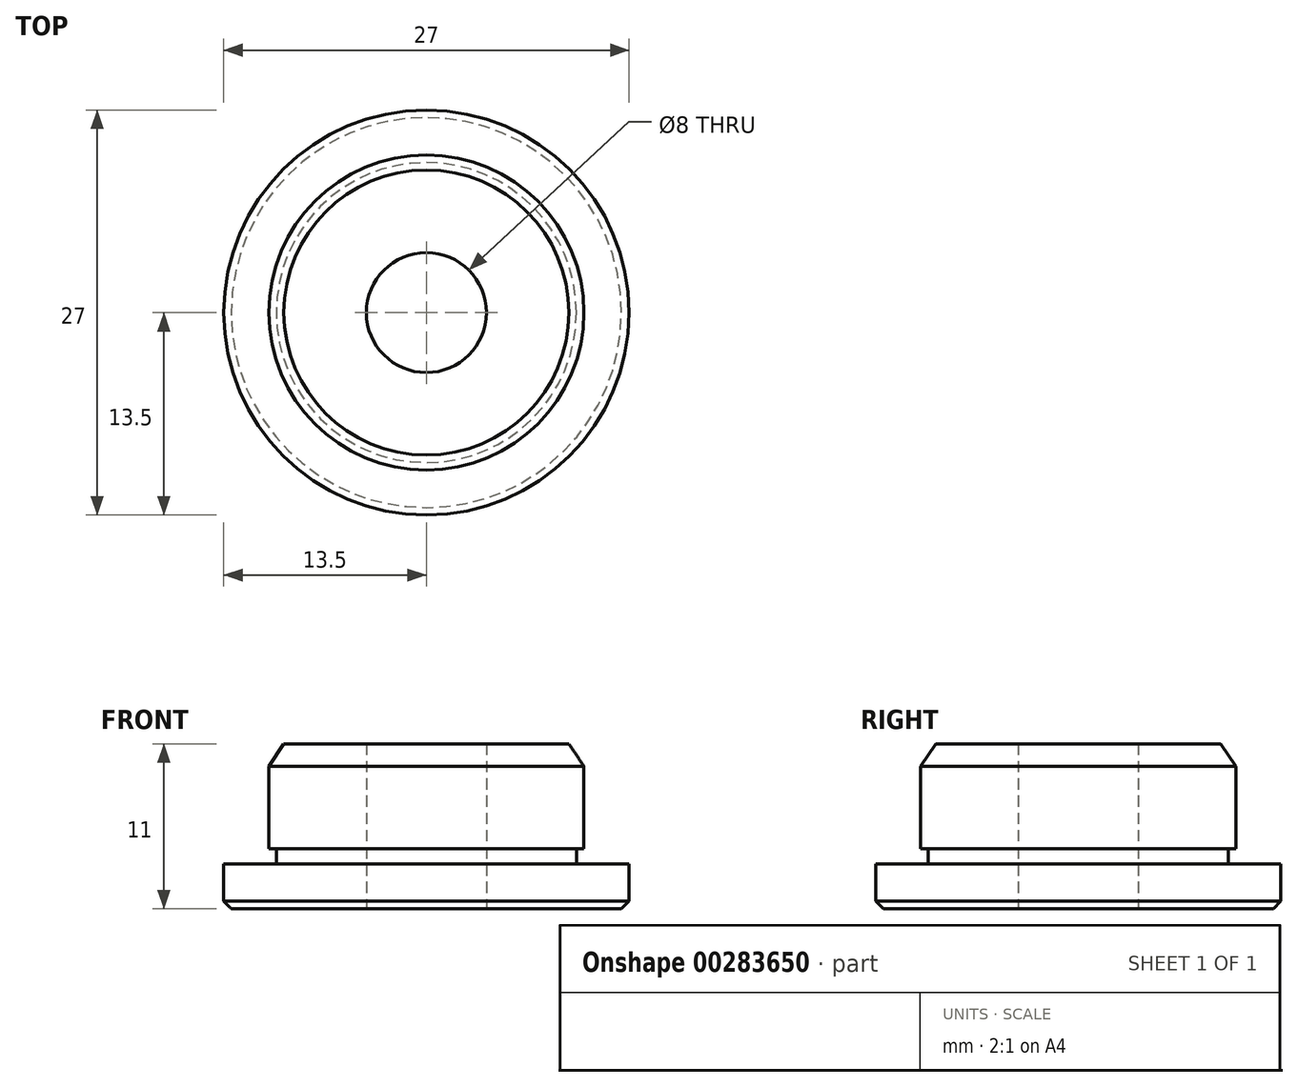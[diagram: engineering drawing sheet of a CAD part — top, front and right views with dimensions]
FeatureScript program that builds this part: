
annotation { "Feature Type Name" : "Feature", "Feature Type Description" : "" }
export const myFeature = defineFeature(function(context is Context, id is Id, definition is map)
    precondition{}
    {
        {
            var Q0;
            Q0=qCreatedBy(makeId("Front.planeOp"),FACE);
            var sketch = newSketch(context, id + "F0", { "sketchPlane" : qUnion([Q0])});
            skLineSegment(sketch, "E0", {"start": v(0, 0) * mm, "end": v(0, 5.57) * mm, "construction": true});
            skLineSegment(sketch, "E1", {"start": v(4, 11) * mm, "end": v(4, 0) * mm});
            skLineSegment(sketch, "E2", {"start": v(4, 0) * mm, "end": v(13.5, 0) * mm});
            skLineSegment(sketch, "E3", {"start": v(13.5, 0) * mm, "end": v(13.5, 3) * mm});
            skLineSegment(sketch, "E4", {"start": v(13.5, 3) * mm, "end": v(10.5, 3) * mm});
            skLineSegment(sketch, "E5", {"start": v(10.5, 3) * mm, "end": v(10.5, 11) * mm});
            skLineSegment(sketch, "E6", {"start": v(10.5, 11) * mm, "end": v(4, 11) * mm});
            skLineSegment(sketch, "E7.MirrorCS", {"start": v(-4, 11) * mm, "end": v(-4, 0) * mm, "construction": true});
            skLineSegment(sketch, "E8.MirrorCS", {"start": v(-4, 0) * mm, "end": v(-13.5, 0) * mm, "construction": true});
            skLineSegment(sketch, "E9.MirrorCS", {"start": v(-10.5, 11) * mm, "end": v(-4, 11) * mm, "construction": true});
            skLineSegment(sketch, "E10.MirrorCS", {"start": v(-13.5, 3) * mm, "end": v(-10.5, 3) * mm, "construction": true});
            skLineSegment(sketch, "E11.MirrorCS", {"start": v(-10.5, 3) * mm, "end": v(-10.5, 11) * mm, "construction": true});
            skLineSegment(sketch, "E12.MirrorCS", {"start": v(-13.5, 0) * mm, "end": v(-13.5, 3) * mm, "construction": true});
            skSolve(sketch);
        }
        {
            var Q0;
            Q0 = qSketchRegion(id + "F0", true);
            var Q1;
            Q1=sQuery(id+"F0.wireOp",EDGE,"E0");
            revolve(context, id + "F1", {"entities" : qUnion([Q0]), "axis" : qUnion([Q1]), "revolveType" : RevolveType.FULL});
        }
        {
            var Q0;
            Q0=makeQuery(id+"F1.opRevolve","SWEPT_EDGE",EDGE,{"disambiguationData":[OSD([sQuery(id+"F0.wireOp",EDGE,"E5"),sQuery(id+"F0.wireOp",EDGE,"E6")])]});
            chamfer(context, id + "F2", {"entities" : qUnion([Q0]), "chamferType" : ChamferType.TWO_OFFSETS, "width1" : 1.5 * mm, "oppositeDirection" : false, "width2" : 1 * mm, "tangentPropagation" : true});
        }
        {
            var Q0;
            Q0=makeQuery(id+"F1.opRevolve","SWEPT_EDGE",EDGE,{"disambiguationData":[OSD([sQuery(id+"F0.wireOp",EDGE,"E3"),sQuery(id+"F0.wireOp",EDGE,"E2")])]});
            chamfer(context, id + "F3", {"entities" : qUnion([Q0]), "width" : 0.5 * mm, "tangentPropagation" : true});
        }
        {
            var Q0;
            Q0=qCreatedBy(makeId("Front.planeOp"),FACE);
            var sketch = newSketch(context, id + "F4", { "sketchPlane" : qUnion([Q0])});
            skLineSegment(sketch, "E13.bottom", {"start": v(10.5, 4) * mm, "end": v(10, 4) * mm});
            skLineSegment(sketch, "E13.top", {"start": v(10.5, 3) * mm, "end": v(10, 3) * mm});
            skLineSegment(sketch, "E13.left", {"start": v(10.5, 4) * mm, "end": v(10.5, 3) * mm});
            skLineSegment(sketch, "E13.right", {"start": v(10, 4) * mm, "end": v(10, 3) * mm});
            skSolve(sketch);
        }
        {
            var Q0;
            Q0 = qSketchRegion(id + "F4", true);
            var Q1;
            Q1=sQuery(id+"F0.wireOp",EDGE,"E0");
            revolve(context, id + "F5", {"operationType" : NewBodyOperationType.REMOVE, "entities" : qUnion([Q0]), "axis" : qUnion([Q1]), "revolveType" : RevolveType.FULL, "oppositeDirection" : true});
        }
    });
